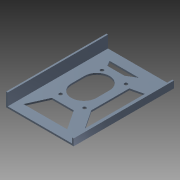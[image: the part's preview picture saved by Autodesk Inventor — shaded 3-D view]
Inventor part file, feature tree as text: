
AUTODESK INVENTOR PART (.ipt)
format: ipt  version: 2013 (Build 170138000, 138)  size: 166,912 bytes
history: native  units: mm
features: sketch x5, extrude x4, other x1, hole x1
ambient origin geometry x1: Origin
feature tree (11):
  other  "ソリッド1"
  extrude  "押し出し1"  Depth=92.0mm
  hole  "穴1"  [1 undecoded]
  extrude  "押し出し3"  Depth=62.0mm
  extrude  "押し出し5"  Depth=31.0mm
  extrude  "押し出し6"  Depth=1.5mm TaperAngle=0.0deg
  sketch  "スケッチ1"
  sketch  "スケッチ3"
  sketch  "スケッチ4"
  sketch  "スケッチ6"
  sketch  "スケッチ7"
note: 1 required parameter value undecoded (feature->parameter linkage not recoverable at this tier; creation-order binding heuristic only, values carry confidence <= 0.55)
